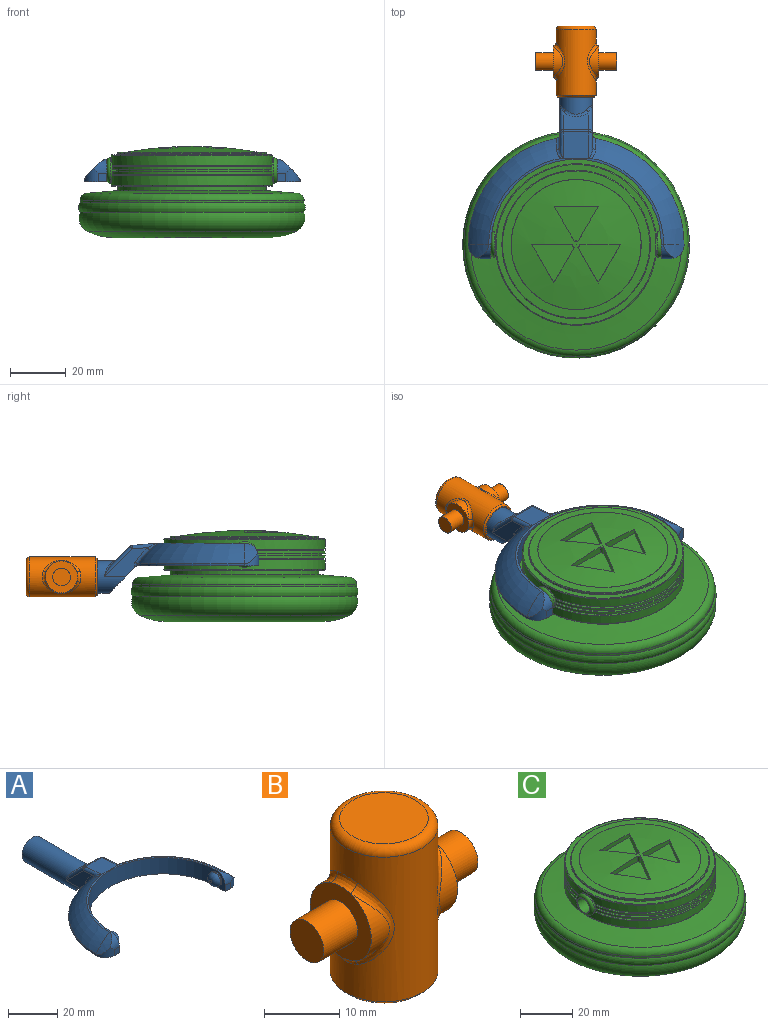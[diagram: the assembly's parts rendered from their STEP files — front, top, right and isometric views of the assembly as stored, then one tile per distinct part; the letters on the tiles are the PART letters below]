
ASSEMBLY  parts=3 mates=2
PART A: 48 faces, bbox 77.3x80.8x18.2 mm
  f0: plane 11.99x9.83mm, normal (0,-0.71,-0.71), area 141.5mm2, adj f1,f2,f9,f30,f43,f46
  f1: plane 15.39x10.49mm, normal (-1,0,0), area 63.5mm2, adj f0,f30,f32,f36,f46,f47
  f2: plane 15.39x10.49mm, normal (1,0,0), area 63.5mm2, adj f0,f30,f34,f39,f43,f44
  f3: plane 9.14x6.37mm, normal (0,0.71,0.71), area 67.6mm2, adj f35,f36,f39,f40
  f4: cylinder r=38.61mm len=37.99mm, axis (0,0,-1), area 42.6mm2, adj f6,f9,f17,f46,f47
  f5: torus R=19.3mm, axis (0,0,-1), area 507.8mm2, adj f10,f11,f12,f29,f42,f44
  f6: torus R=19.3mm, axis (0,0,-1), area 507.8mm2, adj f4,f11,f15,f28,f45,f47
  f7: cylinder r=30.48mm len=60.96mm, axis (0,0,-1), area 746.6mm2, adj f8,f9,f11,f14,f21,f24
  f8: plane 8.13x5.08mm, normal (-1,0,0), area 19.9mm2, adj f7,f9,f13,f19,f24
  f9: plane 77.22x43.73mm, normal (0,0,-1), area 956.2mm2, adj f0,f4,f7,f8,f10,f13,f14,f16
  f10: cylinder r=38.61mm len=37.99mm, axis (0,0,-1), area 42.6mm2, adj f5,f9,f20,f43,f44
  f11: plane 62.55x30.95mm, normal (0,0,1), area 75mm2, adj f5,f6,f7,f18,f19,f27
  f12: cylinder r=22.71mm len=7.33mm, axis (0,1,0), area 24.8mm2, adj f5,f19,f20
  f13: plane 3.05x3.05mm, normal (0,-1,0), area 9.3mm2, adj f8,f9,f19,f20
  f14: plane 8.13x5.08mm, normal (1,0,0), area 19.9mm2, adj f7,f9,f16,f18,f21
  f15: cylinder r=22.71mm len=7.33mm, axis (0,1,0), area 24.8mm2, adj f6,f17,f18
  f16: plane 3.05x3.05mm, normal (0,-1,0), area 9.3mm2, adj f9,f14,f17,f18
  f17: cylinder r=5.08mm len=5.08mm, axis (0,0,-1), area 21.9mm2, adj f4,f9,f15,f16,f18
  f18: cylinder r=5.08mm len=5.08mm, axis (-1,0,0), area 21.9mm2, adj f11,f14,f15,f16,f17
  f19: cylinder r=5.08mm len=5.08mm, axis (-1,0,0), area 21.9mm2, adj f8,f11,f12,f13,f20
  f20: cylinder r=5.08mm len=5.08mm, axis (0,0,-1), area 21.9mm2, adj f9,f10,f12,f13,f19
  f21: cylinder r=3.17mm len=6.35mm, axis (-1,0,0), area 12.7mm2, adj f7,f14,f23
  f22: plane 1.27x1.27mm, normal (1,0,0), area 1.3mm2, adj f23
  f23: torus R=0.64mm, axis (1,0,0), area 56.5mm2, adj f21,f22
  f24: cylinder r=3.17mm len=6.35mm, axis (1,0,0), area 12.7mm2, adj f7,f8,f26
  f25: plane 1.27x1.27mm, normal (-1,0,0), area 1.3mm2, adj f26
  f26: torus R=0.64mm, axis (-1,0,0), area 56.5mm2, adj f24,f25
  f27: plane 9.86x9.36mm, normal (0,0.09,1), area 85.6mm2, adj f11,f28,f29,f32,f34,f35,f42,f45
  f28: plane 1.04x0.17mm, normal (0,-1,0), area 0mm2, adj f6,f27,f45
  f29: plane 1.04x0.17mm, normal (0,-1,0), area 0mm2, adj f5,f27,f42
  f30: cylinder r=5.84mm len=33.01mm, axis (0,-1,0), area 1029.7mm2, adj f0,f1,f2,f31,f38,f40,f41
  f31: plane 11.68x11.68mm, normal (0,1,0), area 107.2mm2, adj f30
  f32: cylinder r=1.27mm len=9.13mm, axis (0,-1,0.09), area 14.4mm2, adj f1,f27,f33,f45
  f33: sphere r=1.27mm, area 1.5mm2, adj f32,f35,f36
  f34: cylinder r=1.27mm len=9.13mm, axis (0,1,-0.09), area 14.4mm2, adj f2,f27,f37,f42
  f35: cylinder r=1.27mm len=9.14mm, axis (-1,0,0), area 8.1mm2, adj f3,f27,f33,f37
  f36: cylinder r=1.27mm len=10.91mm, axis (0,-0.71,0.71), area 23.1mm2, adj f1,f3,f33,f38
  f37: sphere r=1.27mm, area 1.5mm2, adj f34,f35,f39
  f38: bspline ~4.55x2.75mm, area 2.3mm2, adj f30,f36,f40
  f39: cylinder r=1.27mm len=10.91mm, axis (0,0.71,-0.71), area 23.1mm2, adj f2,f3,f37,f41
  f40: bspline ~9.14x2.56mm, area 10.7mm2, adj f3,f30,f38,f41
  f41: bspline ~5.23x3.53mm, area 2.3mm2, adj f30,f39,f40
  f42: bspline ~4.62x3.14mm, area 5.2mm2, adj f5,f27,f29,f34,f44
  f43: cylinder r=1.27mm len=1.74mm, axis (0,0,-1), area 1.9mm2, adj f0,f2,f9,f10,f44
  f44: bspline ~8.6x7.86mm, area 11.9mm2, adj f2,f5,f10,f42,f43
  f45: bspline ~4.62x3.14mm, area 5.2mm2, adj f6,f27,f28,f32,f47
  f46: cylinder r=1.27mm len=1.74mm, axis (0,0,-1), area 1.9mm2, adj f0,f1,f4,f9,f47
  f47: bspline ~8.6x7.86mm, area 11.9mm2, adj f1,f4,f6,f45,f46
PART B: 25 faces, bbox 28.9x15.5x25.4 mm
  f0: cylinder r=5.71mm len=10.81mm, axis (-1,0,0), area 26.2mm2, adj f5,f15
  f1: cylinder r=5.71mm len=10.81mm, axis (-1,0,0), area 26.2mm2, adj f8,f11
  f2: cylinder r=7.14mm len=23.5mm, axis (0,0,-1), area 763.2mm2, adj f9,f10,f11,f12,f13,f14,f15,f16
  f3: plane 11.75x11.75mm, normal (0,0,1), area 108.4mm2, adj f17
  f4: plane 13.02x13.02mm, normal (0,0,-1), area 16.3mm2, adj f22,f24
  f5: plane 11.46x11.46mm, normal (1,0,0), area 70.9mm2, adj f0,f6,f13,f16,f18
  f6: cylinder r=5.71mm len=10.81mm, axis (-1,0,0), area 26.2mm2, adj f5,f14
  f7: cylinder r=5.71mm len=10.81mm, axis (-1,0,0), area 26.2mm2, adj f8,f10
  f8: plane 11.46x11.46mm, normal (-1,0,0), area 70.9mm2, adj f1,f7,f9,f12,f20
  f9: bspline ~4.64x1.73mm, area 6.5mm2, adj f2,f8,f10,f11
  f10: bspline ~13.62x4.91mm, area 20.7mm2, adj f2,f7,f9,f12
  f11: bspline ~13.6x4.87mm, area 20.7mm2, adj f1,f2,f9,f12
  f12: bspline ~4.64x1.73mm, area 6.5mm2, adj f2,f8,f10,f11
  f13: bspline ~4.64x1.73mm, area 6.5mm2, adj f2,f5,f14,f15
  f14: bspline ~13.62x4.91mm, area 20.7mm2, adj f2,f6,f13,f16
  f15: bspline ~13.6x4.87mm, area 20.7mm2, adj f0,f2,f13,f16
  f16: bspline ~4.64x1.73mm, area 6.5mm2, adj f2,f5,f14,f15
  f17: torus R=5.87mm, axis (0,0,1), area 83.8mm2, adj f2,f3
  f18: cylinder r=3.17mm len=6.35mm, axis (-1,0,0), area 126.7mm2, adj f5,f19
  f19: plane 6.35x6.35mm, normal (1,0,0), area 31.7mm2, adj f18
  f20: cylinder r=3.17mm len=6.35mm, axis (1,0,0), area 126.7mm2, adj f8,f21
  f21: plane 6.35x6.35mm, normal (-1,0,0), area 31.7mm2, adj f20
  f22: cylinder r=6.1mm len=22.86mm, axis (0,0,-1), area 875.6mm2, adj f4,f23
  f23: plane 12.19x12.19mm, normal (0,0,-1), area 116.7mm2, adj f22
  f24: cone r=7.14mm half-angle=45deg, axis (0,0,1), area 38.5mm2, adj f2,f4
PART C: 64 faces, bbox 92.6x92.6x32.6 mm
  f0: cylinder r=28.87mm len=57.73mm, axis (0,0,-1), area 595.7mm2, adj f3,f4,f54,f55,f60
  f1: plane 57.06x24.48mm, normal (0,0,-1), area 101.4mm2, adj f6,f8,f54,f55
  f2: plane 57.06x24.48mm, normal (0,0,-1), area 101.4mm2, adj f5,f7,f54,f55
  f3: plane 57.13x24.71mm, normal (0,0,1), area 102mm2, adj f0,f6,f54,f55
  f4: plane 57.13x24.71mm, normal (0,0,1), area 102mm2, adj f0,f5,f54,f55
  f5: cylinder r=27.6mm len=54.56mm, axis (0,0,-1), area 49.6mm2, adj f2,f4,f54,f55
  f6: cylinder r=27.6mm len=54.56mm, axis (0,0,-1), area 49.6mm2, adj f1,f3,f54,f55
  f7: cylinder r=28.87mm len=57.06mm, axis (0,0,-1), area 77.8mm2, adj f2,f10,f54,f55
  f8: cylinder r=28.87mm len=57.06mm, axis (0,0,-1), area 77.8mm2, adj f1,f9,f54,f55
  f9: plane 57.01x24.31mm, normal (0,0,1), area 101mm2, adj f8,f12,f54,f55
  f10: plane 57.01x24.31mm, normal (0,0,1), area 101mm2, adj f7,f11,f54,f55
  f11: cylinder r=27.6mm len=54.44mm, axis (0,0,-1), area 49.2mm2, adj f10,f14,f54,f55
  f12: cylinder r=27.6mm len=54.44mm, axis (0,0,-1), area 49.2mm2, adj f9,f13,f54,f55
  f13: plane 57.01x24.31mm, normal (0,0,-1), area 101mm2, adj f12,f16,f54,f55
  f14: plane 57.01x24.31mm, normal (0,0,-1), area 101mm2, adj f11,f15,f54,f55
  f15: cylinder r=28.87mm len=57.06mm, axis (0,0,-1), area 77.8mm2, adj f14,f20,f54,f55
  f16: cylinder r=28.87mm len=57.06mm, axis (0,0,-1), area 77.8mm2, adj f13,f19,f54,f55
  f17: plane 57.13x24.71mm, normal (0,0,-1), area 102mm2, adj f22,f23,f54,f55
  f18: plane 57.13x24.71mm, normal (0,0,-1), area 102mm2, adj f21,f23,f54,f55
  f19: plane 57.06x24.48mm, normal (0,0,1), area 101.4mm2, adj f16,f22,f54,f55
  f20: plane 57.06x24.48mm, normal (0,0,1), area 101.4mm2, adj f15,f21,f54,f55
  f21: cylinder r=27.6mm len=54.56mm, axis (0,0,-1), area 49.6mm2, adj f18,f20,f54,f55
  f22: cylinder r=27.6mm len=54.56mm, axis (0,0,-1), area 49.6mm2, adj f17,f19,f54,f55
  f23: cylinder r=28.87mm len=57.73mm, axis (0,0,-1), area 595.8mm2, adj f17,f18,f54,f55,f61
  f24: sphere r=135.39mm, area 1385.3mm2, adj f38,f39,f40,f41,f43,f44,f45,f46
  f25: plane 35.89x35.89mm, normal (0,0,-1), area 1011.4mm2, adj f26
  f26: torus R=19.87mm, axis (0,0,-1), area 1349mm2, adj f25,f27
  f27: torus R=28.1mm, axis (0,0,-1), area 3469.3mm2, adj f26,f28
  f28: torus R=35.11mm, axis (0,0,-1), area 1969.7mm2, adj f27,f29
  f29: torus R=37.53mm, axis (0,0,-1), area 918.4mm2, adj f28,f30
  f30: cylinder r=40.06mm len=80.11mm, axis (0,0,-1), area 213.3mm2, adj f29,f34
  f31: cone r=26.57mm half-angle=85deg, axis (0,0,-1), area 2265mm2, adj f32,f34
  f32: cylinder r=26.57mm len=53.14mm, axis (0,0,-1), area 265mm2, adj f31,f33
  f33: plane 57.23x57.23mm, normal (0,0,-1), area 354.5mm2, adj f32,f60
  f34: torus R=37.52mm, axis (0,0,1), area 928.6mm2, adj f30,f31
  f35: cone r=26.57mm half-angle=87deg, axis (0,0,-1), area 475.4mm2, adj f62,f63
  f36: cylinder r=26.57mm len=53.14mm, axis (0,0,-1), area 92.3mm2, adj f37,f62
  f37: plane 57.23x57.23mm, normal (0,0,1), area 354.5mm2, adj f36,f61
  f38: cylinder r=1.27mm len=2.53mm, axis (0,0,1), area 3.4mm2, adj f24,f39,f41,f42
  f39: plane 12.67x7.27mm, normal (0.87,0.5,0), area 32.2mm2, adj f24,f38,f40,f42
  f40: plane 13.73x7.98mm, normal (-0.86,0.5,0), area 28mm2, adj f24,f39,f41,f42
  f41: plane 14.61x2.53mm, normal (0,-1,0), area 32.2mm2, adj f24,f38,f40,f42
  f42: plane 15.24x13.77mm, normal (0,0,1), area 108.3mm2, adj f38,f39,f40,f41
  f43: plane 14.61x2.53mm, normal (0,-1,0), area 32.2mm2, adj f24,f44,f46,f47
  f44: plane 13.77x7.9mm, normal (0.87,0.5,0), area 28mm2, adj f24,f43,f45,f47
  f45: plane 12.63x7.34mm, normal (-0.86,0.5,0), area 32.2mm2, adj f24,f44,f46,f47
  f46: cylinder r=1.27mm len=2.53mm, axis (0,0,1), area 3.4mm2, adj f24,f43,f45,f47
  f47: plane 15.24x13.77mm, normal (0,0,1), area 108.3mm2, adj f43,f44,f45,f46
  f48: cylinder r=1.27mm len=2.53mm, axis (0,0,1), area 3.4mm2, adj f24,f49,f51,f52
  f49: plane 12.63x7.34mm, normal (-0.86,0.5,0), area 32.2mm2, adj f24,f48,f50,f52
  f50: plane 15.88x1.84mm, normal (0,-1,0), area 28mm2, adj f24,f49,f51,f52
  f51: plane 12.67x7.27mm, normal (0.87,0.5,0), area 32.2mm2, adj f24,f48,f50,f52
  f52: plane 15.88x12.67mm, normal (0,0,1), area 108.3mm2, adj f48,f49,f50,f51
  f53: plane 6.6x6.6mm, normal (1,0,0), area 2.6mm2, adj f58,f59
  f54: cylinder r=4.57mm len=9.14mm, axis (-1,0,0), area 20.2mm2, adj f0,f1,f2,f3,f4,f5,f6,f7
  f55: cylinder r=4.57mm len=9.14mm, axis (-1,0,0), area 20.2mm2, adj f0,f1,f2,f3,f4,f5,f6,f7
  f56: plane 6.6x6.6mm, normal (-1,0,0), area 2.6mm2, adj f57,f59
  f57: torus R=3.3mm, axis (1,0,0), area 51.5mm2, adj f55,f56
  f58: torus R=3.3mm, axis (1,0,0), area 51.5mm2, adj f53,f54
  f59: cylinder r=3.17mm len=60.96mm, axis (1,0,0), area 1216.1mm2, adj f53,f56
  f60: torus R=28.61mm, axis (0,0,1), area 72.1mm2, adj f0,f33
  f61: torus R=28.61mm, axis (0,0,-1), area 72.1mm2, adj f23,f37
  f62: torus R=26.31mm, axis (0,0,1), area 64.2mm2, adj f35,f36
  f63: torus R=23.29mm, axis (0,0,1), area 4.5mm2, adj f24,f35
PLACE A t=(32.34,27.52,20.85)mm
PLACE B rot(axis=(-1,0,0),90deg) t=(32.34,80.3,16.88)mm
PLACE C t=(32.34,27.52,33.52)mm
MATE revolute A.f24 <-> C.f54  axis (-1,0,0) through (62.82,27.52,24.92)mm
MATE revolute B.f2 <-> A.f30  axis (0,-1,0) through (32.34,103.16,16.88)mm
